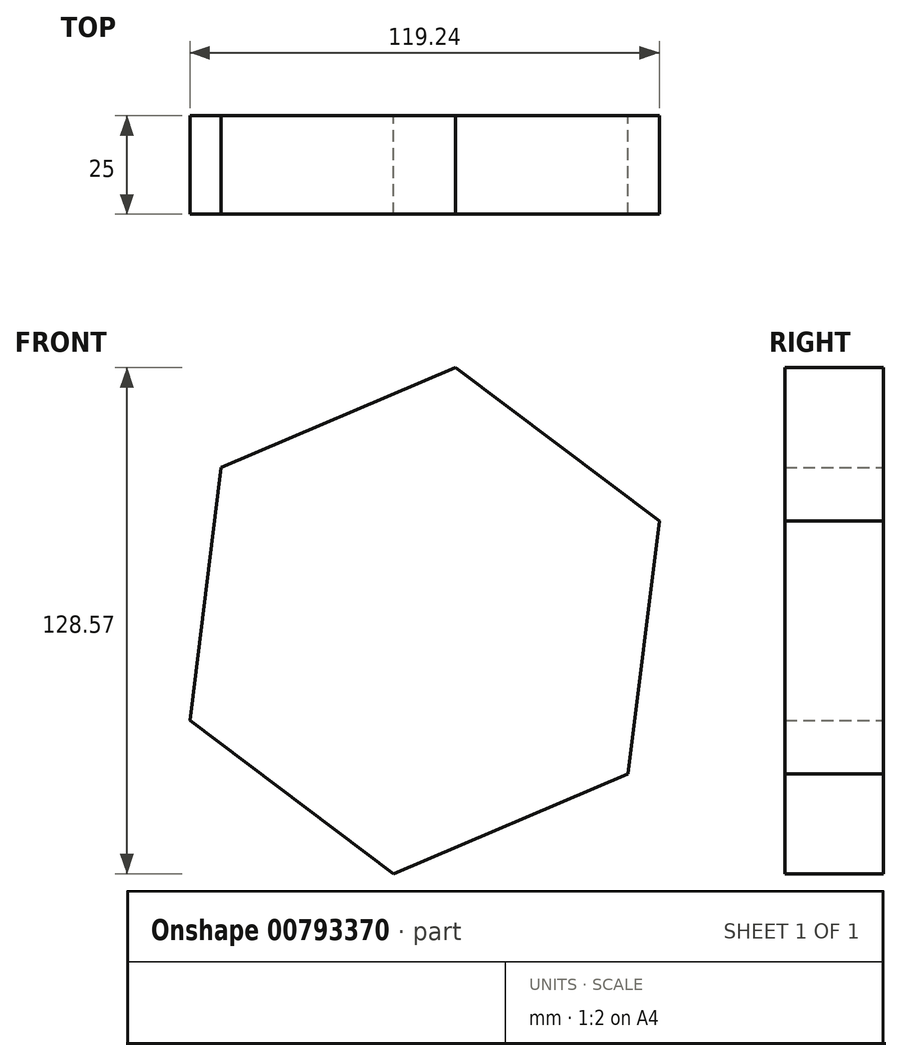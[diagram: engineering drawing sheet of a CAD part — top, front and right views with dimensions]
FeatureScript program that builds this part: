
annotation { "Feature Type Name" : "Feature", "Feature Type Description" : "" }
export const myFeature = defineFeature(function(context is Context, id is Id, definition is map)
    precondition{}
    {
        {
            var Q0;
            Q0=qCreatedBy(makeId("Front.planeOp"),FACE);
            var sketch = newSketch(context, id + "F0", { "sketchPlane" : qUnion([Q0])});
            skCircle(sketch, "E0.cCircle", {"center": v(-83.9, 5.15) * mm, "radius": 56.09 * mm, "construction": true});
            skLineSegment(sketch, "E0.0", {"start": v(-76, 69.44) * mm, "end": v(-24.28, 30.46) * mm});
            skLineSegment(sketch, "E0.1", {"start": v(-24.28, 30.46) * mm, "end": v(-32.17, -33.82) * mm});
            skLineSegment(sketch, "E0.2", {"start": v(-32.17, -33.82) * mm, "end": v(-91.79, -59.13) * mm});
            skLineSegment(sketch, "E0.3", {"start": v(-91.79, -59.13) * mm, "end": v(-143.52, -20.16) * mm});
            skLineSegment(sketch, "E0.4", {"start": v(-143.52, -20.16) * mm, "end": v(-135.62, 44.13) * mm});
            skLineSegment(sketch, "E0.5", {"start": v(-135.62, 44.13) * mm, "end": v(-76, 69.44) * mm});
            skPoint(sketch, "E0.0.midPoint", {"position": v(-50.14, 49.95) * mm});
            skSolve(sketch);
        }
        {
            var Q0;
            Q0 = qSketchRegion(id + "F0", true);
            extrude(context, id + "F1", {"entities" : qUnion([Q0]), "depth" : 25 * mm, "offsetDistance" : 25 * mm});
        }
    });
